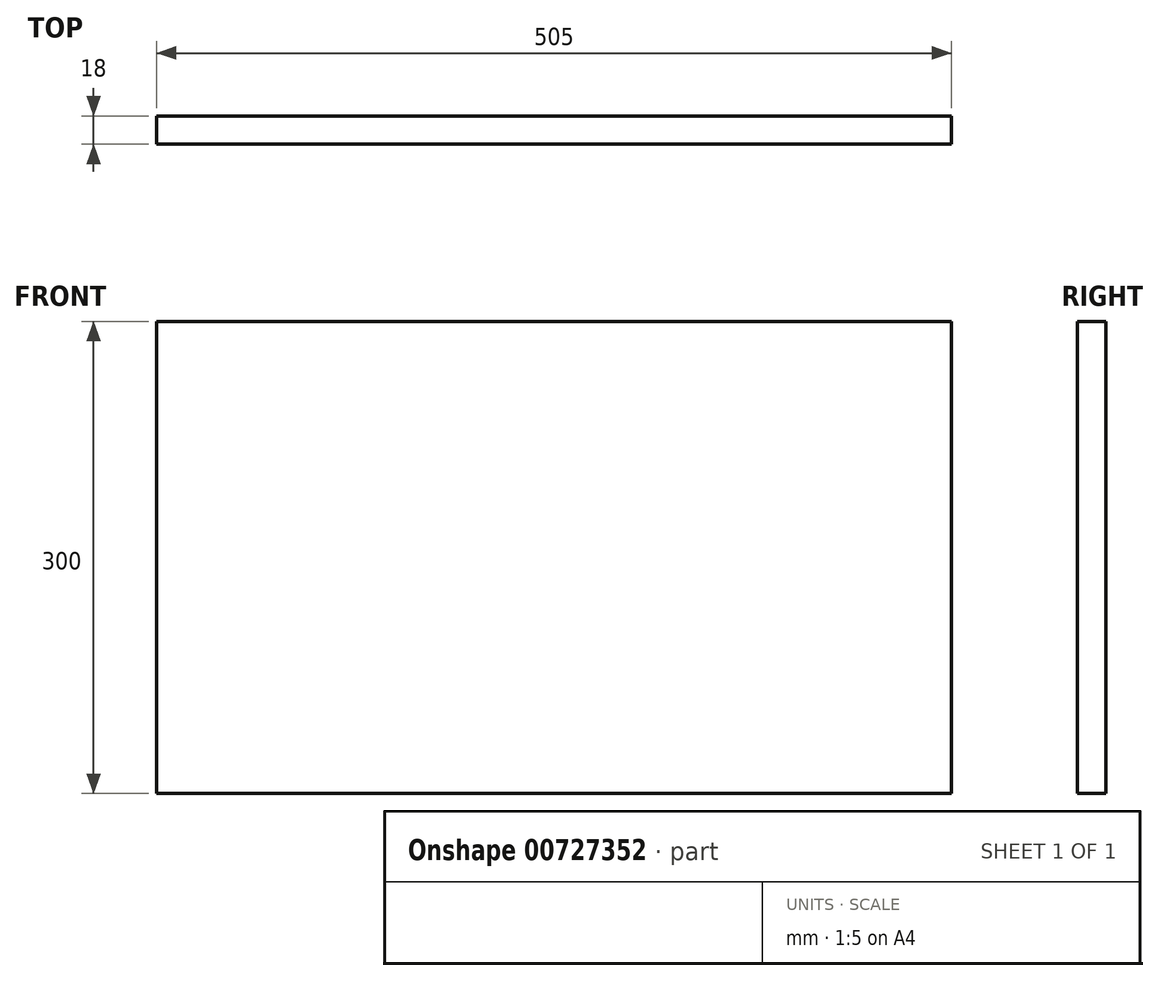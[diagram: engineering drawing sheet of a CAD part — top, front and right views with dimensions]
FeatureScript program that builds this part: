
annotation { "Feature Type Name" : "Feature", "Feature Type Description" : "" }
export const myFeature = defineFeature(function(context is Context, id is Id, definition is map)
    precondition{}
    {
        {
            var Q0;
            Q0=qCreatedBy(makeId("Front.planeOp"),FACE);
            var sketch = newSketch(context, id + "F0", { "sketchPlane" : qUnion([Q0])});
            skLineSegment(sketch, "E0.bottom", {"start": v(0, 0) * mm, "end": v(505, 0) * mm});
            skLineSegment(sketch, "E0.top", {"start": v(0, 300) * mm, "end": v(505, 300) * mm});
            skLineSegment(sketch, "E0.left", {"start": v(0, 0) * mm, "end": v(0, 300) * mm});
            skLineSegment(sketch, "E0.right", {"start": v(505, 0) * mm, "end": v(505, 300) * mm});
            skSolve(sketch);
        }
        {
            var Q0;
            Q0=qSketchRegion(id+"F0",true);
            extrude(context, id + "F1", {"entities" : qUnion([Q0]), "depth" : 18 * mm, "offsetDistance" : 25 * mm});
        }
    });
